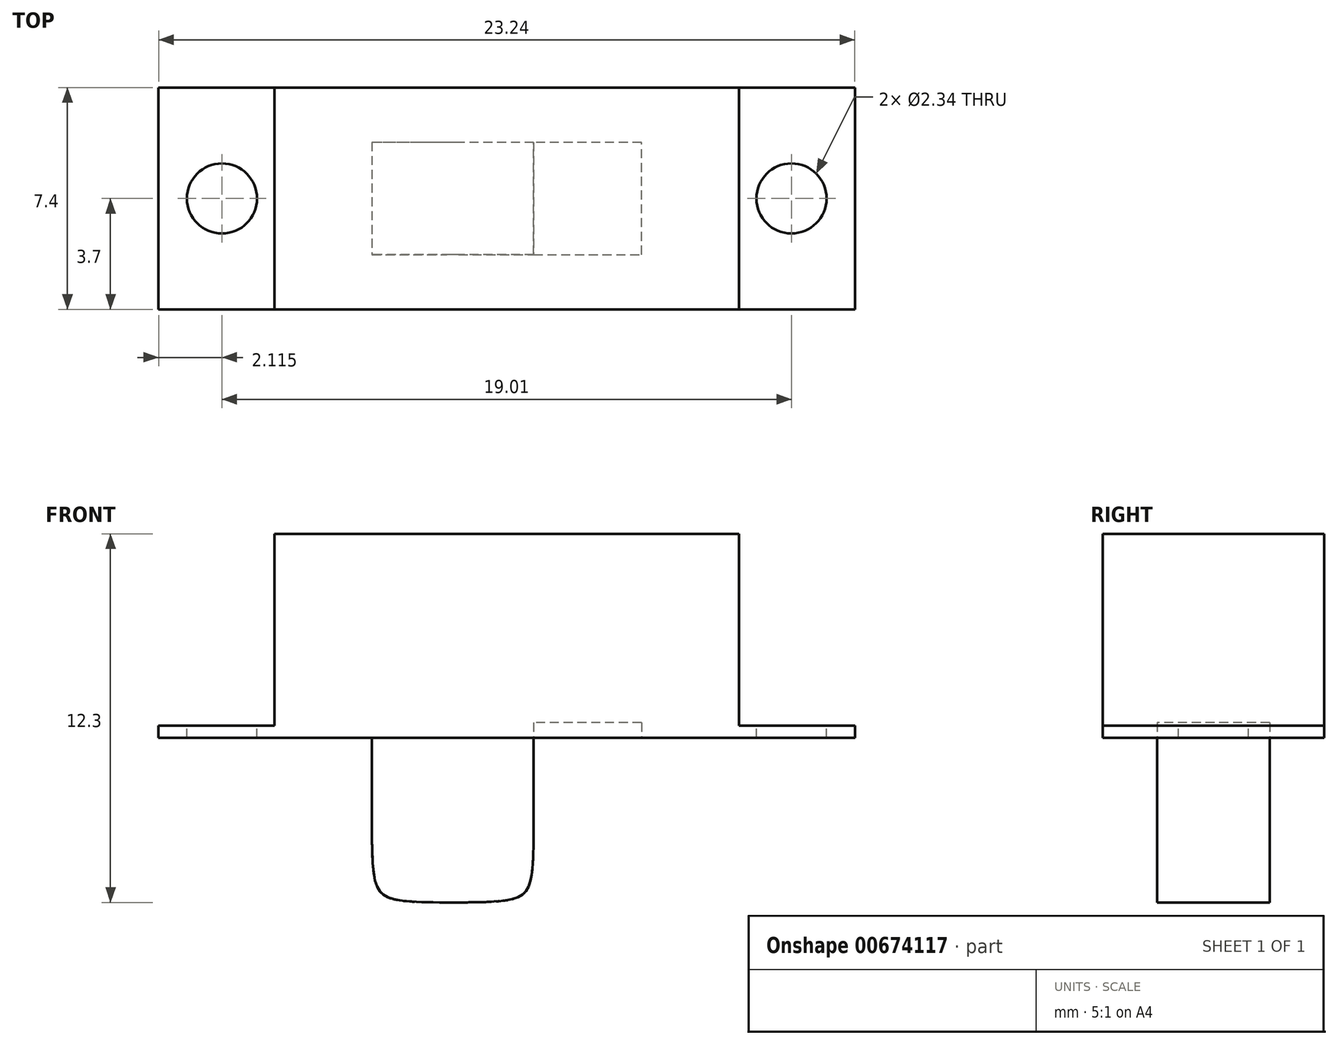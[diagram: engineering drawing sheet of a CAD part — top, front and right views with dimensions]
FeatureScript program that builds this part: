
annotation { "Feature Type Name" : "Feature", "Feature Type Description" : "" }
export const myFeature = defineFeature(function(context is Context, id is Id, definition is map)
    precondition{}
    {
        {
            var Q0;
            Q0=qCreatedBy(makeId("Top.planeOp"),FACE);
            var sketch = newSketch(context, id + "F0", { "sketchPlane" : qUnion([Q0])});
            skLineSegment(sketch, "E0.bottom", {"start": v(7.75, -3.7) * mm, "end": v(-7.75, -3.7) * mm});
            skLineSegment(sketch, "E0.top", {"start": v(7.75, 3.7) * mm, "end": v(-7.75, 3.7) * mm});
            skLineSegment(sketch, "E0.left", {"start": v(7.75, -3.7) * mm, "end": v(7.75, 3.7) * mm});
            skLineSegment(sketch, "E0.right", {"start": v(-7.75, -3.7) * mm, "end": v(-7.75, 3.7) * mm});
            skPoint(sketch, "E0.middle", {"position": v(0, 0) * mm});
            skLineSegment(sketch, "E1", {"start": v(7.75, 3.7) * mm, "end": v(11.62, 3.7) * mm});
            skLineSegment(sketch, "E2", {"start": v(11.62, 3.7) * mm, "end": v(11.62, -3.7) * mm});
            skLineSegment(sketch, "E3", {"start": v(11.62, -3.7) * mm, "end": v(7.75, -3.7) * mm});
            skLineSegment(sketch, "E4.MirrorCS", {"start": v(-7.75, 3.7) * mm, "end": v(-11.62, 3.7) * mm});
            skLineSegment(sketch, "E5.MirrorCS", {"start": v(-11.62, -3.7) * mm, "end": v(-7.75, -3.7) * mm});
            skLineSegment(sketch, "E6.MirrorCS", {"start": v(-11.62, 3.7) * mm, "end": v(-11.62, -3.7) * mm});
            skCircle(sketch, "E7", {"center": v(9.5, 0) * mm, "radius": 1.17 * mm});
            skCircle(sketch, "E8.MirrorC", {"center": v(-9.5, 0) * mm, "radius": 1.17 * mm});
            skSolve(sketch);
        }
        {
            var Q0;
            Q0=makeQuery(id+"F0.imprint","IMPRINT",FACE,{"disambiguationData":[TD([[makeQuery(id+"F0.imprint","IMPRINT",EDGE,{"derivedFrom":sQuery(id+"F0.wireOp",EDGE,"E0.right")}),1.0]])]});
            var Q1;
            Q1=makeQuery(id+"F0.imprint","IMPRINT",FACE,{"disambiguationData":[TD([[makeQuery(id+"F0.imprint","IMPRINT",EDGE,{"derivedFrom":sQuery(id+"F0.wireOp",EDGE,"E0.bottom")}),-1.0]])]});
            var Q2;
            Q2=makeQuery(id+"F0.imprint","IMPRINT",FACE,{"disambiguationData":[TD([[makeQuery(id+"F0.imprint","IMPRINT",EDGE,{"derivedFrom":sQuery(id+"F0.wireOp",EDGE,"E0.left")}),-1.0]])]});
            extrude(context, id + "F1", {"entities" : qUnion([Q0, Q1, Q2]), "oppositeDirection" : true, "depth" : 0.4 * mm, "offsetDistance" : 25 * mm});
        }
        {
            var Q0;
            Q0=makeQuery(id+"F0.imprint","IMPRINT",FACE,{"disambiguationData":[TD([[makeQuery(id+"F0.imprint","IMPRINT",EDGE,{"derivedFrom":sQuery(id+"F0.wireOp",EDGE,"E0.bottom")}),-1.0]])]});
            extrude(context, id + "F2", {"entities" : qUnion([Q0]), "operationType" : NewBodyOperationType.ADD, "depth" : 6.4 * mm, "offsetDistance" : 25 * mm});
        }
        {
            var Q0;
            Q0=makeQuery(id+"F1.opExtrude","CAP_FACE",FACE,{"disambiguationData":[OSD([sQuery(id+"F0.wireOp",EDGE,"E0.bottom"),sQuery(id+"F0.wireOp",EDGE,"E0.top"),sQuery(id+"F0.wireOp",EDGE,"E1"),sQuery(id+"F0.wireOp",EDGE,"E2"),sQuery(id+"F0.wireOp",EDGE,"E3"),sQuery(id+"F0.wireOp",EDGE,"E4.MirrorCS"),sQuery(id+"F0.wireOp",EDGE,"E5.MirrorCS"),sQuery(id+"F0.wireOp",EDGE,"E6.MirrorCS"),sQuery(id+"F0.wireOp",EDGE,"E7"),sQuery(id+"F0.wireOp",EDGE,"E8.MirrorC")])],"isStart":false});
            var sketch = newSketch(context, id + "F3", { "sketchPlane" : qUnion([Q0])});
            skLineSegment(sketch, "E9.bottom", {"start": v(0.9, -1.88) * mm, "end": v(-4.5, -1.88) * mm});
            skLineSegment(sketch, "E9.top", {"start": v(0.9, 1.88) * mm, "end": v(-4.5, 1.88) * mm});
            skLineSegment(sketch, "E9.left", {"start": v(0.9, -1.88) * mm, "end": v(0.9, 1.87) * mm});
            skLineSegment(sketch, "E9.right", {"start": v(-4.5, -1.88) * mm, "end": v(-4.5, 1.87) * mm});
            skLineSegment(sketch, "E10", {"start": v(0.9, 1.88) * mm, "end": v(4.5, 1.88) * mm});
            skLineSegment(sketch, "E11", {"start": v(4.5, 1.88) * mm, "end": v(4.5, -1.88) * mm});
            skLineSegment(sketch, "E12", {"start": v(4.5, -1.88) * mm, "end": v(0.9, -1.88) * mm});
            skSolve(sketch);
        }
        {
            var Q0;
            Q0=makeQuery(id+"F3.imprint","IMPRINT",FACE,{"disambiguationData":[TD([[makeQuery(id+"F3.imprint","IMPRINT",EDGE,{"derivedFrom":sQuery(id+"F3.wireOp",EDGE,"E9.left")}),-1.0]])]});
            extrude(context, id + "F4", {"entities" : qUnion([Q0]), "operationType" : NewBodyOperationType.REMOVE, "oppositeDirection" : true, "depth" : .5 * mm, "offsetDistance" : 25 * mm});
        }
        {
            var Q0;
            Q0=makeQuery(id+"F3.imprint","IMPRINT",FACE,{"disambiguationData":[TD([[makeQuery(id+"F3.imprint","IMPRINT",EDGE,{"derivedFrom":sQuery(id+"F3.wireOp",EDGE,"E9.bottom")}),-1.0]])]});
            extrude(context, id + "F5", {"entities" : qUnion([Q0]), "operationType" : NewBodyOperationType.ADD, "depth" : 5.5 * mm, "offsetDistance" : 25 * mm});
        }
        {
            var Q0;
            Q0=makeQuery(id+"F5.opExtrude","CAP_EDGE",EDGE,{"disambiguationData":[OSD([sQuery(id+"F3.wireOp",EDGE,"E9.right")])],"isStart":false});
            var Q1;
            Q1=makeQuery(id+"F5.opExtrude","CAP_EDGE",EDGE,{"disambiguationData":[OSD([sQuery(id+"F3.wireOp",EDGE,"E9.left")])],"isStart":false});
            fillet(context, id + "F6", {"entities" : qUnion([Q0, Q1]), "radius" : 2.5 * mm, "tangentPropagation" : true, "rho" : .75, "crossSection" : FilletCrossSection.CONIC, "allowEdgeOverflow" : false});
        }
        {
            var Q0;
            Q0=makeQuery(id+"F3.imprint","IMPRINT",FACE,{"disambiguationData":[TD([[makeQuery(id+"F3.imprint","IMPRINT",EDGE,{"derivedFrom":sQuery(id+"F3.wireOp",EDGE,"E9.left")}),-1.0]])]});
            extrude(context, id + "F7", {"entities" : qUnion([Q0]), "operationType" : NewBodyOperationType.REMOVE, "oppositeDirection" : true, "depth" : .5 * mm, "offsetDistance" : 25 * mm});
        }
    });
